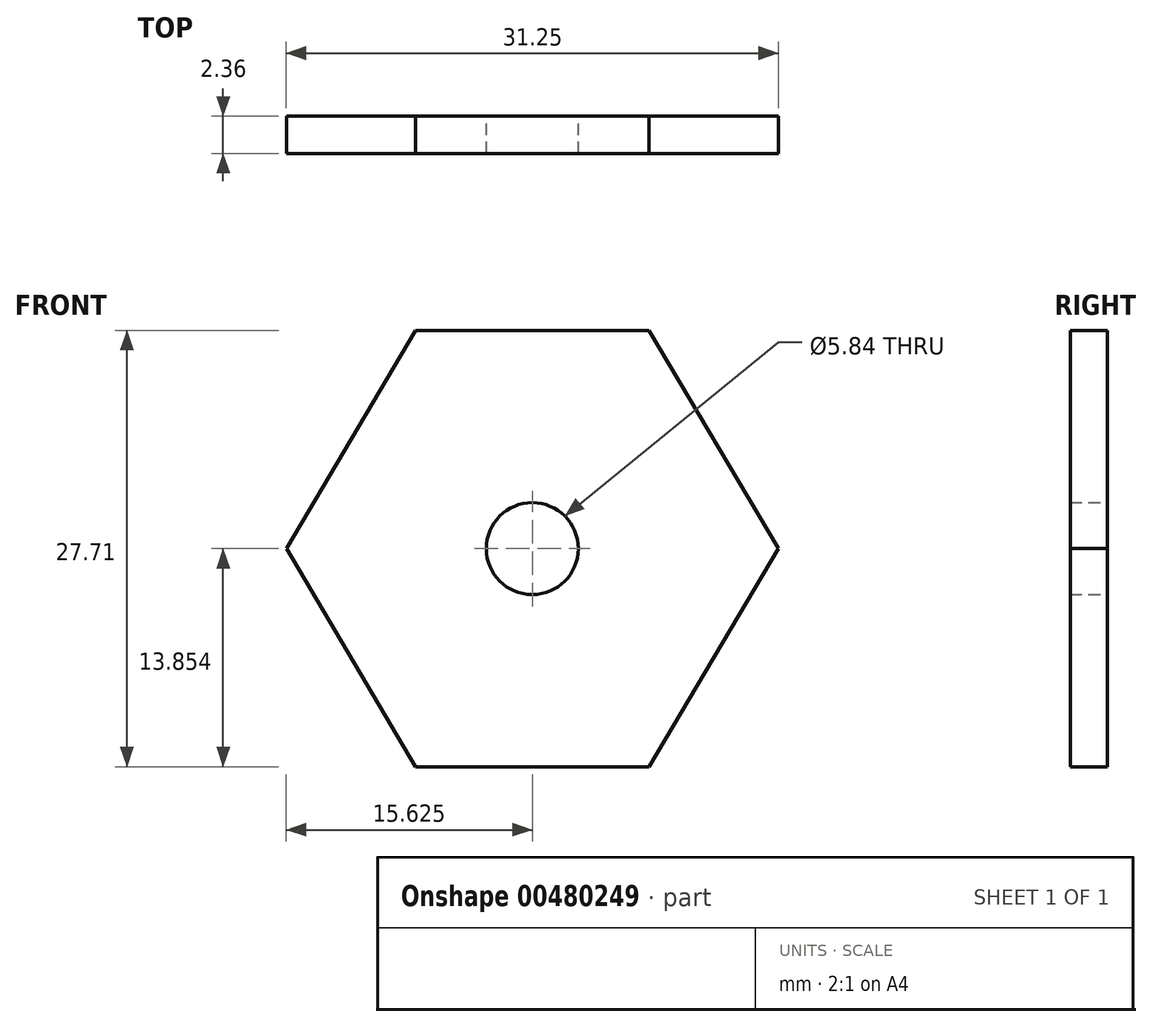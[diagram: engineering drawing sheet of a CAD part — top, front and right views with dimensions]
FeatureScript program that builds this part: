
annotation { "Feature Type Name" : "Feature", "Feature Type Description" : "" }
export const myFeature = defineFeature(function(context is Context, id is Id, definition is map)
    precondition{}
    {
        {
            var Q0;
            Q0=qCreatedBy(makeId("Front.planeOp"),FACE);
            var sketch = newSketch(context, id + "F0", { "sketchPlane" : qUnion([Q0])});
            skLineSegment(sketch, "E0", {"start": v(-14.45, -9.23) * mm, "end": v(-14.45, 18.48) * mm});
            skLineSegment(sketch, "E1", {"start": v(-37.4, 27.04) * mm, "end": v(-6.16, 27.04) * mm});
            skLineSegment(sketch, "E2", {"start": v(-14.45, 4.62) * mm, "end": v(1.18, 4.62) * mm});
            skPoint(sketch, "E2.endSnap0", {"position": v(-14.45, 4.62) * mm});
            skLineSegment(sketch, "E3", {"start": v(-14.45, 4.62) * mm, "end": v(-30.07, 4.62) * mm});
            skLineSegment(sketch, "E4", {"start": v(-14.45, 18.48) * mm, "end": v(-7.03, 18.48) * mm});
            skLineSegment(sketch, "E5", {"start": v(-14.45, 18.48) * mm, "end": v(-21.86, 18.48) * mm});
            skLineSegment(sketch, "E6", {"start": v(-14.45, -9.23) * mm, "end": v(-7.03, -9.23) * mm});
            skLineSegment(sketch, "E7", {"start": v(-14.45, -9.23) * mm, "end": v(-21.86, -9.23) * mm});
            skLineSegment(sketch, "E8", {"start": v(-30.07, 4.62) * mm, "end": v(-21.86, -9.23) * mm});
            skLineSegment(sketch, "E9", {"start": v(-7.03, -9.23) * mm, "end": v(1.18, 4.62) * mm});
            skLineSegment(sketch, "E10", {"start": v(-7.03, 18.48) * mm, "end": v(1.18, 4.62) * mm});
            skLineSegment(sketch, "E11", {"start": v(-21.86, 18.48) * mm, "end": v(-30.07, 4.62) * mm});
            skCircle(sketch, "E12", {"center": v(-14.45, 4.62) * mm, "radius": 2.92 * mm});
            skSolve(sketch);
        }
        {
            var Q0;
            Q0=qSketchRegion(id+"F0",true);
            extrude(context, id + "F1", {"entities" : qUnion([Q0]), "depth" : 2.36 * mm, "offsetDistance" : 25.4 * mm});
        }
    });
